# Revit family: Skylight_Velux-Sun_Tunnels-TGC-14in
name_source: partatom
category: Specialty Equipment
revit_build: Autodesk Revit 2015 (Build: 20140606_1530(x64)
units: mm (PartAtom-declared; Revit-internal decimal feet)

## types (3) — shared parameters
Assembly Code = B3020110
BIMobject category = Skylights
BIMobject category code = windows-skylights
BIMobject main category = Windows
BIMobject main category code = windows
Brand url = http://www.veluxusa.com
Default Elevation = 0' - 0"
Description = Sun Tunnel Skylight
Design country = United States
Dome Material = Acrylic or Polycarbonate - Velux - Clear Impact Modified
Duct Diameter = 1' - 2"
Duct Material = Metal - Velux - 99% reflective Aluminum, 0.016" - 0.02" thick
Edition number = 1
Flashing Length = 2' - 5"
Flashing Radius High = 0' - 8 11/16"
Flashing Radius Low = 0' - 10 9/32"
Flashing Width = 2' - 5"
Installation instructions = http://dd1.domwebx.com
Manufacturer = VELUX
Manufacturer name = VELUX US
Masterformat 2014 Code = 08 62 23
Masterformat 2014 Description = Tubular Skylights
Model = TGC 014
Nominal height = 0' - 0"
Nominal width = 0' - 0"
OmniClass Code = 23-17 17 13 21
OmniClass Description = Tubular Skylights
Performance Data = http://www.veluxusa.com
Product Documentation Link = http://www.veluxusa.com
Product Guid = cdbf27fe-351a-48a2-a6e5-29f6cb321b6b
Product Page URL = http://www.veluxusa.com
Product SKU = velux-skylight-tgc
Product certification = http://www.veluxusa.com
Product data url = https://bimobject.com
Product family = Windows
Product group = Skylights
Product url = http://www.veluxusa.com
QR code = http://bimobject.com
Rough Width = 1' - 2 1/2"
Technical description = http://dd1.domwebx.com
UNSPSC Code = 30171803
URL = http://www.veluxusa.com
Uniclass 1.4 Code = L4145
Uniclass 1.4 Description = Skylights
Uniclass 2015 Code = Pr_30_59_72_77
Uniclass 2015 Name = Skylights
Void R1 = 0' - 8 21/32"
Void R2 = 0' - 10 1/4"
Weight Net (Kg) = 0
Width (Nominal) = 1' - 2"

## per-type parameters (varying)
| type | Flashing Extension 0012 | Flashing Extension 0036 | Flashing Material | Frame Material |
| TGC - 14" | No | No | Metal - Velux - G90 Galvanized Sheet | Metal - Velux - G90 Galvanized Sheet |
| TGC - 14" with 12" Extension | Yes | No | Metal - Velux - 99% reflective Aluminum, 0.016" - 0.02" thick | Metal - Velux - 99% reflective Aluminum, 0.016" - 0.02" thick |
| TGC - 14" with 36" Extension | No | Yes | Metal - Velux - 99% reflective Aluminum, 0.016" - 0.02" thick | Metal - Velux - 99% reflective Aluminum, 0.016" - 0.02" thick |

## geometry (parser evidence)
native form markers: Sweep x8
no freeform markers — native parametric forms only
